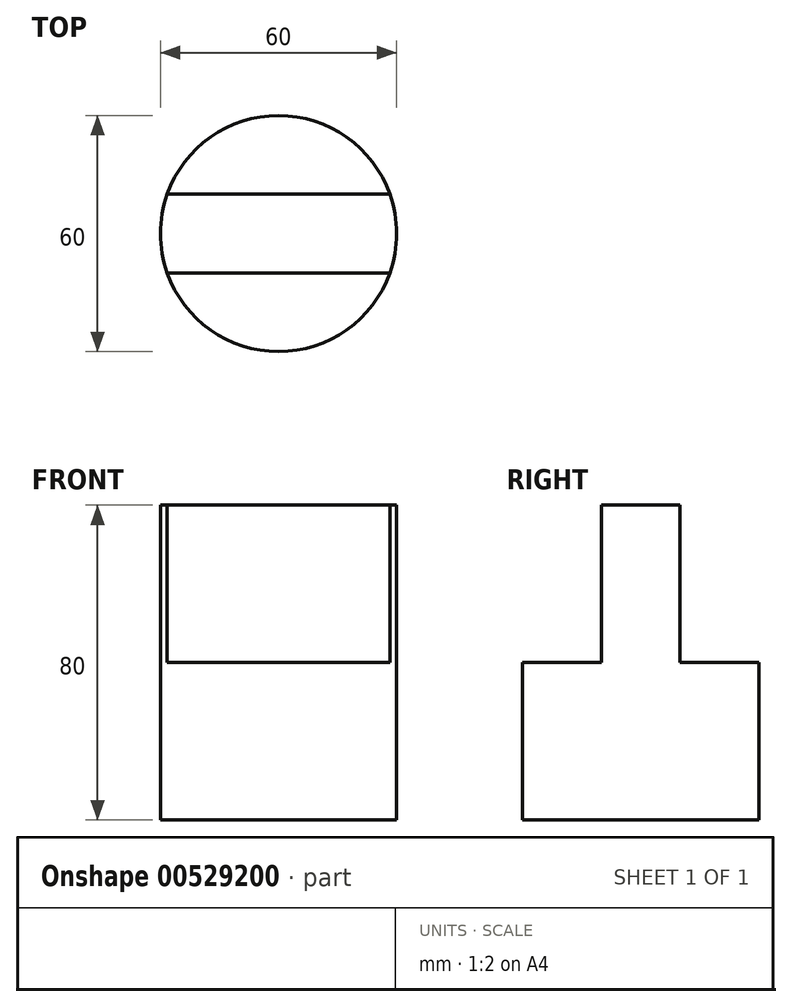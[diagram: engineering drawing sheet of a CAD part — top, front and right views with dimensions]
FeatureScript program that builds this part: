
annotation { "Feature Type Name" : "Feature", "Feature Type Description" : "" }
export const myFeature = defineFeature(function(context is Context, id is Id, definition is map)
    precondition{}
    {
        {
            var Q0;
            Q0=qCreatedBy(makeId("Top.planeOp"),FACE);
            var sketch = newSketch(context, id + "F0", { "sketchPlane" : qUnion([Q0])});
            skCircle(sketch, "E0", {"center": v(0, 0) * mm, "radius": 30 * mm});
            skSolve(sketch);
        }
        {
            var Q0;
            Q0=makeQuery(id+"F0.imprint","IMPRINT",FACE,{"disambiguationData":[TD([[makeQuery(id+"F0.imprint","IMPRINT",EDGE,{"derivedFrom":sQuery(id+"F0.wireOp",EDGE,"E0")}),1.0]])]});
            extrude(context, id + "F1", {"entities" : qUnion([Q0]), "endBound" : BoundingType.SYMMETRIC, "depth" : 80 * mm, "offsetDistance" : 25 * mm});
        }
        {
            var Q0;
            Q0=makeQuery(id+"F1.opExtrude","CAP_FACE",FACE,{"disambiguationData":[OSD([sQuery(id+"F0.wireOp",EDGE,"E0")])],"isStart":false});
            var sketch = newSketch(context, id + "F2", { "sketchPlane" : qUnion([Q0])});
            skCircle(sketch, "E1.0", {"center": v(0, 0) * mm, "radius": 30 * mm});
            skLineSegment(sketch, "E2", {"start": v(-30, 0) * mm, "end": v(30, 0) * mm, "construction": true});
            skLineSegment(sketch, "E3", {"start": v(28.28, 10) * mm, "end": v(-28.28, 10) * mm});
            skLineSegment(sketch, "E4", {"start": v(28.28, -10) * mm, "end": v(-28.28, -10) * mm});
            skSolve(sketch);
        }
        {
            var Q0;
            {var subQ0=sQuery(id+"F2.wireOp",EDGE,"E3");Q0=makeQuery(id+"F2.imprint","IMPRINT",FACE,{"disambiguationData":[TD([[makeQuery(id+"F2.imprint","IMPRINT",EDGE,{"derivedFrom":subQ0}),-1.0]])]});}
            var Q1;
            {var subQ0=sQuery(id+"F2.wireOp",EDGE,"E4");Q1=makeQuery(id+"F2.imprint","IMPRINT",FACE,{"disambiguationData":[TD([[makeQuery(id+"F2.imprint","IMPRINT",EDGE,{"derivedFrom":subQ0}),1.0]])]});}
            extrude(context, id + "F3", {"entities" : qUnion([Q0, Q1]), "operationType" : NewBodyOperationType.REMOVE, "oppositeDirection" : true, "depth" : 40 * mm, "offsetDistance" : 25 * mm});
        }
    });
